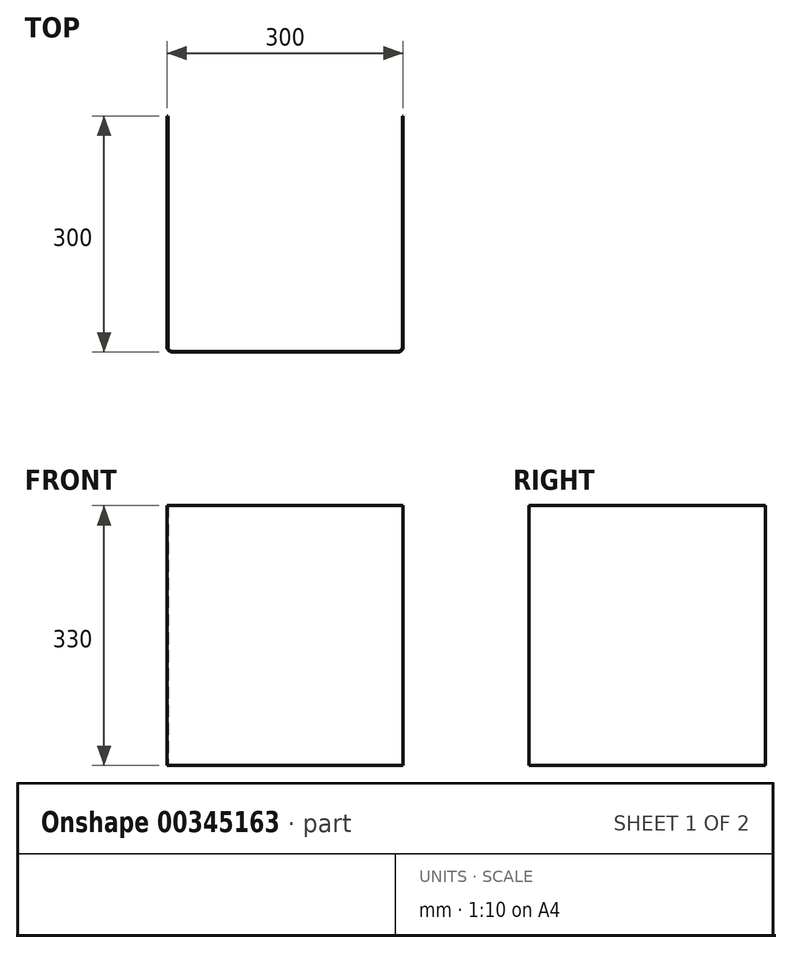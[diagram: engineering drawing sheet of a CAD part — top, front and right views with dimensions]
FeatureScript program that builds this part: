
annotation { "Feature Type Name" : "Feature", "Feature Type Description" : "" }
export const myFeature = defineFeature(function(context is Context, id is Id, definition is map)
    precondition{}
    {
        {
            var Q0;
            Q0=qCreatedBy(makeId("Top.planeOp"),FACE);
            var sketch = newSketch(context, id + "F0", { "sketchPlane" : qUnion([Q0])});
            skLineSegment(sketch, "E0.bottom", {"start": v(0, 0) * mm, "end": v(56.56, 0) * mm});
            skLineSegment(sketch, "E0.top", {"start": v(0, 35.83) * mm, "end": v(56.56, 35.83) * mm});
            skLineSegment(sketch, "E0.left", {"start": v(0, 0) * mm, "end": v(0, 35.83) * mm});
            skLineSegment(sketch, "E0.right", {"start": v(56.56, 0) * mm, "end": v(56.56, 35.83) * mm});
            skSolve(sketch);
        }
        {
            var Q0;
            Q0=makeQuery(id+"F0.imprint","IMPRINT",FACE,{"disambiguationData":[TD([[makeQuery(id+"F0.imprint","IMPRINT",EDGE,{"derivedFrom":sQuery(id+"F0.wireOp",EDGE,"E0.bottom")}),1.0]])]});
            extrude(context, id + "F1", {"entities" : qUnion([Q0]), "depth" : 330 * mm});
        }
        {
            var Q0;
            Q0=makeQuery(id+"F1.opExtrude","SWEPT_FACE",FACE,{"disambiguationData":[OSD([sQuery(id+"F0.wireOp",EDGE,"E0.left")])]});
            extrude(context, id + "F2", {"entities" : qUnion([Q0]), "operationType" : NewBodyOperationType.ADD, "oppositeDirection" : true, "depth" : 300 * mm});
        }
        {
            var Q0;
            {var subQ0=sQuery(id+"F0.wireOp",EDGE,"E0.bottom");Q0=makeQuery(id+"F2.boolean.opBoolean","MERGE",FACE,{"derivedFrom":[makeQuery(id+"F1.opExtrude","SWEPT_FACE",FACE,{"disambiguationData":[OSD([subQ0])]}),makeQuery(id+"F2.opExtrude","SWEPT_FACE",FACE,{"disambiguationData":[OSD([subQ0,sQuery(id+"F0.wireOp",EDGE,"E0.left")])]})]});}
            extrude(context, id + "F3", {"entities" : qUnion([Q0]), "operationType" : NewBodyOperationType.ADD, "oppositeDirection" : true, "depth" : 300 * mm});
        }
        {
            var Q0;
            Q0=makeQuery(id+"F1.opExtrude","SWEPT_EDGE",EDGE,{"disambiguationData":[OSD([sQuery(id+"F0.wireOp",EDGE,"E0.bottom"),sQuery(id+"F0.wireOp",EDGE,"E0.left")])]});
            var Q1;
            Q1=makeQuery(id+"F2.opExtrude","CAP_EDGE",EDGE,{"disambiguationData":[OSD([sQuery(id+"F0.wireOp",EDGE,"E0.bottom"),sQuery(id+"F0.wireOp",EDGE,"E0.left")])],"isStart":false});
            fillet(context, id + "F4", {"entities" : qUnion([Q0, Q1]), "radius" : 7 * mm, "tangentPropagation" : true, "allowEdgeOverflow" : false});
        }
        {
            var Q0;
            {var subQ0=sQuery(id+"F0.wireOp",EDGE,"E0.left");var subQ1=sQuery(id+"F0.wireOp",EDGE,"E0.bottom");Q0=makeQuery(id+"F3.boolean.opBoolean","MERGE",FACE,{"derivedFrom":[makeQuery(id+"F2.boolean.opBoolean","MERGE",FACE,{"derivedFrom":[makeQuery(id+"F1.opExtrude","CAP_FACE",FACE,{"disambiguationData":[OSD([subQ1,sQuery(id+"F0.wireOp",EDGE,"E0.top"),subQ0,sQuery(id+"F0.wireOp",EDGE,"E0.right")])],"isStart":false}),makeQuery(id+"F2.opExtrude","SWEPT_FACE",FACE,{"disambiguationData":[OSD([subQ0]),TDD([makeQuery(id+"F1.opExtrude","CAP_EDGE",EDGE,{"disambiguationData":[OSD([subQ0])],"isStart":false})])]})]}),makeQuery(id+"F3.opExtrude","SWEPT_FACE",FACE,{"disambiguationData":[OSD([subQ1,subQ0]),TDD([makeQuery(id+"F2.boolean.opBoolean","MERGE",EDGE,{"derivedFrom":[makeQuery(id+"F1.opExtrude","CAP_EDGE",EDGE,{"disambiguationData":[OSD([subQ1])],"isStart":false}),makeQuery(id+"F2.opExtrude","SWEPT_EDGE",EDGE,{"disambiguationData":[OSD([subQ1,subQ0]),TDD([makeQuery(id+"F1.opExtrude","CAP_VERTEX",VERTEX,{"disambiguationData":[OSD([subQ1,subQ0])],"isStart":false})])]})]})])]})]});}
            var Q1;
            Q1=makeQuery(id+"F3.opExtrude","CAP_FACE",FACE,{"disambiguationData":[OSD([sQuery(id+"F0.wireOp",EDGE,"E0.bottom"),sQuery(id+"F0.wireOp",EDGE,"E0.left")])],"isStart":false});
            var Q2;
            {var subQ0=sQuery(id+"F0.wireOp",EDGE,"E0.left");var subQ1=sQuery(id+"F0.wireOp",EDGE,"E0.bottom");Q2=makeQuery(id+"F3.boolean.opBoolean","MERGE",FACE,{"derivedFrom":[makeQuery(id+"F2.boolean.opBoolean","MERGE",FACE,{"derivedFrom":[makeQuery(id+"F1.opExtrude","CAP_FACE",FACE,{"disambiguationData":[OSD([subQ1,sQuery(id+"F0.wireOp",EDGE,"E0.top"),subQ0,sQuery(id+"F0.wireOp",EDGE,"E0.right")])],"isStart":true}),makeQuery(id+"F2.opExtrude","SWEPT_FACE",FACE,{"disambiguationData":[OSD([subQ0]),TDD([makeQuery(id+"F1.opExtrude","CAP_EDGE",EDGE,{"disambiguationData":[OSD([subQ0])],"isStart":true})])]})]}),makeQuery(id+"F3.opExtrude","SWEPT_FACE",FACE,{"disambiguationData":[OSD([subQ1,subQ0]),TDD([makeQuery(id+"F2.boolean.opBoolean","MERGE",EDGE,{"derivedFrom":[makeQuery(id+"F1.opExtrude","CAP_EDGE",EDGE,{"disambiguationData":[OSD([subQ1])],"isStart":true}),makeQuery(id+"F2.opExtrude","SWEPT_EDGE",EDGE,{"disambiguationData":[OSD([subQ1,subQ0]),TDD([makeQuery(id+"F1.opExtrude","CAP_VERTEX",VERTEX,{"disambiguationData":[OSD([subQ1,subQ0])],"isStart":true})])]})]})])]})]});}
            shell(context, id + "F5", {"entities" : qUnion([Q0, Q1, Q2]), "thickness" : 1 * mm});
        }
    });
